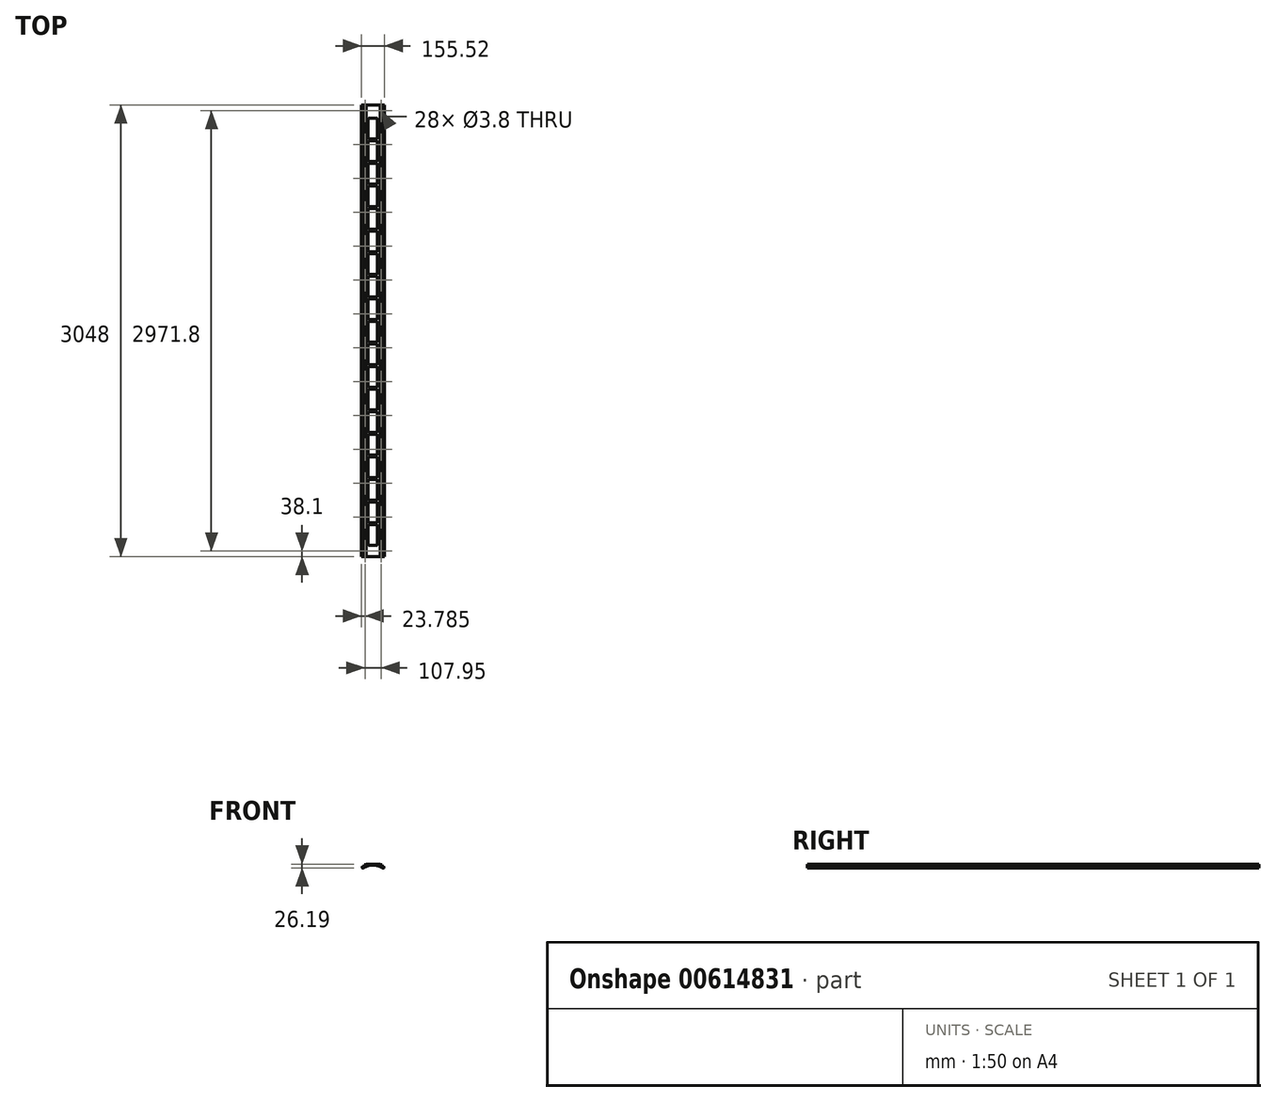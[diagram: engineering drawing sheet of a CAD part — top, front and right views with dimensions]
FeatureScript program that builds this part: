
annotation { "Feature Type Name" : "Feature", "Feature Type Description" : "" }
export const myFeature = defineFeature(function(context is Context, id is Id, definition is map)
    precondition{}
    {
        {
            var Q0;
            Q0=qCreatedBy(makeId("Front.planeOp"),FACE);
            var sketch = newSketch(context, id + "F0", { "sketchPlane" : qUnion([Q0])});
            skLineSegment(sketch, "E0", {"start": v(0, 0) * mm, "end": v(-47.62, 0) * mm});
            skLineSegment(sketch, "E1", {"start": v(-60.33, -4.76) * mm, "end": v(-60.33, -9.52) * mm});
            skArc(sketch, "E2", {"start": v(62.37, -26.2) * mm, "mid": v(0, -6.35) * mm, "end": v(-62.37, -26.2) * mm});
            skLineSegment(sketch, "E3", {"start": v(-60.33, -9.53) * mm, "end": v(-77.76, -22.36) * mm});
            skLineSegment(sketch, "E4", {"start": v(-77.76, -22.36) * mm, "end": v(-73.17, -22.36) * mm});
            skLineSegment(sketch, "E5", {"start": v(-73.17, -22.36) * mm, "end": v(-73.17, -26.2) * mm});
            skLineSegment(sketch, "E6", {"start": v(-73.17, -26.2) * mm, "end": v(-62.37, -26.2) * mm});
            skLineSegment(sketch, "E7.MirrorCS", {"start": v(0, 0) * mm, "end": v(47.62, 0) * mm});
            skLineSegment(sketch, "E8.MirrorCS", {"start": v(60.33, -4.76) * mm, "end": v(60.33, -9.53) * mm});
            skLineSegment(sketch, "E9.MirrorCS", {"start": v(60.33, -9.52) * mm, "end": v(77.76, -22.36) * mm});
            skLineSegment(sketch, "E10.MirrorCS", {"start": v(77.76, -22.36) * mm, "end": v(73.17, -22.36) * mm});
            skLineSegment(sketch, "E11.MirrorCS", {"start": v(73.17, -22.36) * mm, "end": v(73.17, -26.2) * mm});
            skLineSegment(sketch, "E12.MirrorCS", {"start": v(73.17, -26.2) * mm, "end": v(62.37, -26.2) * mm});
            skLineSegment(sketch, "E13", {"start": v(-47.62, 0) * mm, "end": v(-47.62, -4.76) * mm});
            skLineSegment(sketch, "E14", {"start": v(-47.62, -4.76) * mm, "end": v(-60.33, -4.76) * mm});
            skPoint(sketch, "E15.orphan", {"position": v(-60.33, 0) * mm});
            skLineSegment(sketch, "E16.MirrorCS", {"start": v(47.62, 0) * mm, "end": v(47.62, -4.76) * mm});
            skLineSegment(sketch, "E17.MirrorCS", {"start": v(47.62, -4.76) * mm, "end": v(60.33, -4.76) * mm});
            skPoint(sketch, "E18.orphan", {"position": v(60.32, 0) * mm});
            skPoint(sketch, "E19.orphan", {"position": v(60.33, 0) * mm});
            skSolve(sketch);
        }
        {
            var Q0;
            Q0=makeQuery(id+"F0.imprint","IMPRINT",FACE,{"disambiguationData":[TD([[makeQuery(id+"F0.imprint","IMPRINT",EDGE,{"derivedFrom":sQuery(id+"F0.wireOp",EDGE,"E0")}),1.0]])]});
            extrude(context, id + "F1", {"entities" : qUnion([Q0]), "endBound" : BoundingType.SYMMETRIC, "depth" : 3048 * mm, "offsetDistance" : 25.4 * mm});
        }
        {
            var Q0;
            Q0=makeQuery(id+"F1.opExtrude","SWEPT_FACE",FACE,{"disambiguationData":[OSD([sQuery(id+"F0.wireOp",EDGE,"E0"),sQuery(id+"F0.wireOp",EDGE,"E7.MirrorCS")])]});
            var sketch = newSketch(context, id + "F2", { "sketchPlane" : qUnion([Q0])});
            skLineSegment(sketch, "E20.bottom", {"start": v(-32.27, -1447.8) * mm, "end": v(31.23, -1447.8) * mm});
            skLineSegment(sketch, "E20.top", {"start": v(-32.27, -1308.1) * mm, "end": v(31.23, -1308.1) * mm});
            skLineSegment(sketch, "E20.left", {"start": v(-32.27, -1447.8) * mm, "end": v(-32.27, -1308.1) * mm});
            skLineSegment(sketch, "E20.right", {"start": v(31.23, -1447.8) * mm, "end": v(31.23, -1308.1) * mm});
            skLineSegment(sketch, "E21.0.1.0", {"start": v(-32.27, -1295.4) * mm, "end": v(-32.27, -1155.7) * mm});
            skLineSegment(sketch, "E21.0.1.1", {"start": v(-32.27, -1155.7) * mm, "end": v(31.23, -1155.7) * mm});
            skLineSegment(sketch, "E21.0.1.2", {"start": v(31.23, -1295.4) * mm, "end": v(31.23, -1155.7) * mm});
            skLineSegment(sketch, "E21.0.1.3", {"start": v(-32.27, -1295.4) * mm, "end": v(31.23, -1295.4) * mm});
            skLineSegment(sketch, "E21.0.2.0", {"start": v(-32.27, -1143) * mm, "end": v(-32.27, -1003.3) * mm});
            skLineSegment(sketch, "E21.0.2.1", {"start": v(-32.27, -1003.3) * mm, "end": v(31.23, -1003.3) * mm});
            skLineSegment(sketch, "E21.0.2.2", {"start": v(31.23, -1143) * mm, "end": v(31.23, -1003.3) * mm});
            skLineSegment(sketch, "E21.0.2.3", {"start": v(-32.27, -1143) * mm, "end": v(31.23, -1143) * mm});
            skLineSegment(sketch, "E21.0.3.0", {"start": v(-32.27, -990.6) * mm, "end": v(-32.27, -850.9) * mm});
            skLineSegment(sketch, "E21.0.3.1", {"start": v(-32.27, -850.9) * mm, "end": v(31.23, -850.9) * mm});
            skLineSegment(sketch, "E21.0.3.2", {"start": v(31.23, -990.6) * mm, "end": v(31.23, -850.9) * mm});
            skLineSegment(sketch, "E21.0.3.3", {"start": v(-32.27, -990.6) * mm, "end": v(31.23, -990.6) * mm});
            skLineSegment(sketch, "E21.0.4.0", {"start": v(-32.27, -838.2) * mm, "end": v(-32.27, -698.5) * mm});
            skLineSegment(sketch, "E21.0.4.1", {"start": v(-32.27, -698.5) * mm, "end": v(31.23, -698.5) * mm});
            skLineSegment(sketch, "E21.0.4.2", {"start": v(31.23, -838.2) * mm, "end": v(31.23, -698.5) * mm});
            skLineSegment(sketch, "E21.0.4.3", {"start": v(-32.27, -838.2) * mm, "end": v(31.23, -838.2) * mm});
            skLineSegment(sketch, "E21.0.5.0", {"start": v(-32.27, -685.8) * mm, "end": v(-32.27, -546.1) * mm});
            skLineSegment(sketch, "E21.0.5.1", {"start": v(-32.27, -546.1) * mm, "end": v(31.23, -546.1) * mm});
            skLineSegment(sketch, "E21.0.5.2", {"start": v(31.23, -685.8) * mm, "end": v(31.23, -546.1) * mm});
            skLineSegment(sketch, "E21.0.5.3", {"start": v(-32.27, -685.8) * mm, "end": v(31.23, -685.8) * mm});
            skLineSegment(sketch, "E21.0.6.0", {"start": v(-32.27, -533.4) * mm, "end": v(-32.27, -393.7) * mm});
            skLineSegment(sketch, "E21.0.6.1", {"start": v(-32.27, -393.7) * mm, "end": v(31.23, -393.7) * mm});
            skLineSegment(sketch, "E21.0.6.2", {"start": v(31.23, -533.4) * mm, "end": v(31.23, -393.7) * mm});
            skLineSegment(sketch, "E21.0.6.3", {"start": v(-32.27, -533.4) * mm, "end": v(31.23, -533.4) * mm});
            skLineSegment(sketch, "E21.0.7.0", {"start": v(-32.27, -381) * mm, "end": v(-32.27, -241.3) * mm});
            skLineSegment(sketch, "E21.0.7.1", {"start": v(-32.27, -241.3) * mm, "end": v(31.23, -241.3) * mm});
            skLineSegment(sketch, "E21.0.7.2", {"start": v(31.23, -381) * mm, "end": v(31.23, -241.3) * mm});
            skLineSegment(sketch, "E21.0.7.3", {"start": v(-32.27, -381) * mm, "end": v(31.23, -381) * mm});
            skLineSegment(sketch, "E21.0.8.0", {"start": v(-32.27, -228.6) * mm, "end": v(-32.27, -88.9) * mm});
            skLineSegment(sketch, "E21.0.8.1", {"start": v(-32.27, -88.9) * mm, "end": v(31.23, -88.9) * mm});
            skLineSegment(sketch, "E21.0.8.2", {"start": v(31.23, -228.6) * mm, "end": v(31.23, -88.9) * mm});
            skLineSegment(sketch, "E21.0.8.3", {"start": v(-32.27, -228.6) * mm, "end": v(31.23, -228.6) * mm});
            skLineSegment(sketch, "E21.0.9.0", {"start": v(-32.27, -76.2) * mm, "end": v(-32.27, 63.5) * mm});
            skLineSegment(sketch, "E21.0.9.1", {"start": v(-32.27, 63.5) * mm, "end": v(31.23, 63.5) * mm});
            skLineSegment(sketch, "E21.0.9.2", {"start": v(31.23, -76.2) * mm, "end": v(31.23, 63.5) * mm});
            skLineSegment(sketch, "E21.0.9.3", {"start": v(-32.27, -76.2) * mm, "end": v(31.23, -76.2) * mm});
            skLineSegment(sketch, "E21.0.10.0", {"start": v(-32.27, 76.2) * mm, "end": v(-32.27, 215.9) * mm});
            skLineSegment(sketch, "E21.0.10.1", {"start": v(-32.27, 215.9) * mm, "end": v(31.23, 215.9) * mm});
            skLineSegment(sketch, "E21.0.10.2", {"start": v(31.23, 76.2) * mm, "end": v(31.23, 215.9) * mm});
            skLineSegment(sketch, "E21.0.10.3", {"start": v(-32.27, 76.2) * mm, "end": v(31.23, 76.2) * mm});
            skLineSegment(sketch, "E21.0.11.0", {"start": v(-32.27, 228.6) * mm, "end": v(-32.27, 368.3) * mm});
            skLineSegment(sketch, "E21.0.11.1", {"start": v(-32.27, 368.3) * mm, "end": v(31.23, 368.3) * mm});
            skLineSegment(sketch, "E21.0.11.2", {"start": v(31.23, 228.6) * mm, "end": v(31.23, 368.3) * mm});
            skLineSegment(sketch, "E21.0.11.3", {"start": v(-32.27, 228.6) * mm, "end": v(31.23, 228.6) * mm});
            skLineSegment(sketch, "E21.0.12.0", {"start": v(-32.27, 381) * mm, "end": v(-32.27, 520.7) * mm});
            skLineSegment(sketch, "E21.0.12.1", {"start": v(-32.27, 520.7) * mm, "end": v(31.23, 520.7) * mm});
            skLineSegment(sketch, "E21.0.12.2", {"start": v(31.23, 381) * mm, "end": v(31.23, 520.7) * mm});
            skLineSegment(sketch, "E21.0.12.3", {"start": v(-32.27, 381) * mm, "end": v(31.23, 381) * mm});
            skLineSegment(sketch, "E21.0.13.0", {"start": v(-32.27, 533.4) * mm, "end": v(-32.27, 673.1) * mm});
            skLineSegment(sketch, "E21.0.13.1", {"start": v(-32.27, 673.1) * mm, "end": v(31.23, 673.1) * mm});
            skLineSegment(sketch, "E21.0.13.2", {"start": v(31.23, 533.4) * mm, "end": v(31.23, 673.1) * mm});
            skLineSegment(sketch, "E21.0.13.3", {"start": v(-32.27, 533.4) * mm, "end": v(31.23, 533.4) * mm});
            skLineSegment(sketch, "E21.0.14.0", {"start": v(-32.27, 685.8) * mm, "end": v(-32.27, 825.5) * mm});
            skLineSegment(sketch, "E21.0.14.1", {"start": v(-32.27, 825.5) * mm, "end": v(31.23, 825.5) * mm});
            skLineSegment(sketch, "E21.0.14.2", {"start": v(31.23, 685.8) * mm, "end": v(31.23, 825.5) * mm});
            skLineSegment(sketch, "E21.0.14.3", {"start": v(-32.27, 685.8) * mm, "end": v(31.23, 685.8) * mm});
            skLineSegment(sketch, "E21.0.15.0", {"start": v(-32.27, 838.2) * mm, "end": v(-32.27, 977.9) * mm});
            skLineSegment(sketch, "E21.0.15.1", {"start": v(-32.27, 977.9) * mm, "end": v(31.23, 977.9) * mm});
            skLineSegment(sketch, "E21.0.15.2", {"start": v(31.23, 838.2) * mm, "end": v(31.23, 977.9) * mm});
            skLineSegment(sketch, "E21.0.15.3", {"start": v(-32.27, 838.2) * mm, "end": v(31.23, 838.2) * mm});
            skLineSegment(sketch, "E21.0.16.0", {"start": v(-32.27, 990.6) * mm, "end": v(-32.27, 1130.3) * mm});
            skLineSegment(sketch, "E21.0.16.1", {"start": v(-32.27, 1130.3) * mm, "end": v(31.23, 1130.3) * mm});
            skLineSegment(sketch, "E21.0.16.2", {"start": v(31.23, 990.6) * mm, "end": v(31.23, 1130.3) * mm});
            skLineSegment(sketch, "E21.0.16.3", {"start": v(-32.27, 990.6) * mm, "end": v(31.23, 990.6) * mm});
            skLineSegment(sketch, "E21.0.17.0", {"start": v(-32.27, 1143) * mm, "end": v(-32.27, 1282.7) * mm});
            skLineSegment(sketch, "E21.0.17.1", {"start": v(-32.27, 1282.7) * mm, "end": v(31.23, 1282.7) * mm});
            skLineSegment(sketch, "E21.0.17.2", {"start": v(31.23, 1143) * mm, "end": v(31.23, 1282.7) * mm});
            skLineSegment(sketch, "E21.0.17.3", {"start": v(-32.27, 1143) * mm, "end": v(31.23, 1143) * mm});
            skLineSegment(sketch, "E21.0.18.0", {"start": v(-32.27, 1295.4) * mm, "end": v(-32.27, 1435.1) * mm});
            skLineSegment(sketch, "E21.0.18.1", {"start": v(-32.27, 1435.1) * mm, "end": v(31.23, 1435.1) * mm});
            skLineSegment(sketch, "E21.0.18.2", {"start": v(31.23, 1295.4) * mm, "end": v(31.23, 1435.1) * mm});
            skLineSegment(sketch, "E21.0.18.3", {"start": v(-32.27, 1295.4) * mm, "end": v(31.23, 1295.4) * mm});
            skLineSegment(sketch, "E21.0.19.0", {"start": v(-32.27, 1447.8) * mm, "end": v(-32.27, 1587.5) * mm});
            skLineSegment(sketch, "E21.0.19.1", {"start": v(-32.27, 1587.5) * mm, "end": v(31.23, 1587.5) * mm});
            skLineSegment(sketch, "E21.0.19.2", {"start": v(31.23, 1447.8) * mm, "end": v(31.23, 1587.5) * mm});
            skLineSegment(sketch, "E21.0.19.3", {"start": v(-32.27, 1447.8) * mm, "end": v(31.23, 1447.8) * mm});
            skLineSegment(sketch, "E21.direction1", {"start": v(-32.27, -1447.8) * mm, "end": v(-6.87, -1447.8) * mm, "construction": true});
            skLineSegment(sketch, "E21.direction2", {"start": v(-32.27, -1447.8) * mm, "end": v(-32.27, -1295.4) * mm, "construction": true});
            skSolve(sketch);
        }
        {
            var Q0;
            Q0=makeQuery(id+"F2.imprint","IMPRINT",FACE,{"disambiguationData":[TD([[makeQuery(id+"F2.imprint","IMPRINT",EDGE,{"derivedFrom":sQuery(id+"F2.wireOp",EDGE,"E20.bottom")}),1.0]])]});
            var Q1;
            Q1=makeQuery(id+"F2.imprint","IMPRINT",FACE,{"disambiguationData":[TD([[makeQuery(id+"F2.imprint","IMPRINT",EDGE,{"derivedFrom":sQuery(id+"F2.wireOp",EDGE,"E21.0.1.0")}),-1.0]])]});
            var Q2;
            Q2=makeQuery(id+"F2.imprint","IMPRINT",FACE,{"disambiguationData":[TD([[makeQuery(id+"F2.imprint","IMPRINT",EDGE,{"derivedFrom":sQuery(id+"F2.wireOp",EDGE,"E21.0.2.0")}),-1.0]])]});
            var Q3;
            Q3=makeQuery(id+"F2.imprint","IMPRINT",FACE,{"disambiguationData":[TD([[makeQuery(id+"F2.imprint","IMPRINT",EDGE,{"derivedFrom":sQuery(id+"F2.wireOp",EDGE,"E21.0.3.0")}),-1.0]])]});
            var Q4;
            Q4=makeQuery(id+"F2.imprint","IMPRINT",FACE,{"disambiguationData":[TD([[makeQuery(id+"F2.imprint","IMPRINT",EDGE,{"derivedFrom":sQuery(id+"F2.wireOp",EDGE,"E21.0.4.0")}),-1.0]])]});
            var Q5;
            Q5=makeQuery(id+"F2.imprint","IMPRINT",FACE,{"disambiguationData":[TD([[makeQuery(id+"F2.imprint","IMPRINT",EDGE,{"derivedFrom":sQuery(id+"F2.wireOp",EDGE,"E21.0.5.0")}),-1.0]])]});
            var Q6;
            Q6=makeQuery(id+"F2.imprint","IMPRINT",FACE,{"disambiguationData":[TD([[makeQuery(id+"F2.imprint","IMPRINT",EDGE,{"derivedFrom":sQuery(id+"F2.wireOp",EDGE,"E21.0.6.0")}),-1.0]])]});
            var Q7;
            Q7=makeQuery(id+"F2.imprint","IMPRINT",FACE,{"disambiguationData":[TD([[makeQuery(id+"F2.imprint","IMPRINT",EDGE,{"derivedFrom":sQuery(id+"F2.wireOp",EDGE,"E21.0.7.0")}),-1.0]])]});
            var Q8;
            Q8=makeQuery(id+"F2.imprint","IMPRINT",FACE,{"disambiguationData":[TD([[makeQuery(id+"F2.imprint","IMPRINT",EDGE,{"derivedFrom":sQuery(id+"F2.wireOp",EDGE,"E21.0.8.0")}),-1.0]])]});
            var Q9;
            Q9=makeQuery(id+"F2.imprint","IMPRINT",FACE,{"disambiguationData":[TD([[makeQuery(id+"F2.imprint","IMPRINT",EDGE,{"derivedFrom":sQuery(id+"F2.wireOp",EDGE,"E21.0.9.0")}),-1.0]])]});
            var Q10;
            Q10=makeQuery(id+"F2.imprint","IMPRINT",FACE,{"disambiguationData":[TD([[makeQuery(id+"F2.imprint","IMPRINT",EDGE,{"derivedFrom":sQuery(id+"F2.wireOp",EDGE,"E21.0.10.0")}),-1.0]])]});
            var Q11;
            Q11=makeQuery(id+"F2.imprint","IMPRINT",FACE,{"disambiguationData":[TD([[makeQuery(id+"F2.imprint","IMPRINT",EDGE,{"derivedFrom":sQuery(id+"F2.wireOp",EDGE,"E21.0.11.0")}),-1.0]])]});
            var Q12;
            Q12=makeQuery(id+"F2.imprint","IMPRINT",FACE,{"disambiguationData":[TD([[makeQuery(id+"F2.imprint","IMPRINT",EDGE,{"derivedFrom":sQuery(id+"F2.wireOp",EDGE,"E21.0.12.0")}),-1.0]])]});
            var Q13;
            Q13=makeQuery(id+"F2.imprint","IMPRINT",FACE,{"disambiguationData":[TD([[makeQuery(id+"F2.imprint","IMPRINT",EDGE,{"derivedFrom":sQuery(id+"F2.wireOp",EDGE,"E21.0.13.0")}),-1.0]])]});
            var Q14;
            Q14=makeQuery(id+"F2.imprint","IMPRINT",FACE,{"disambiguationData":[TD([[makeQuery(id+"F2.imprint","IMPRINT",EDGE,{"derivedFrom":sQuery(id+"F2.wireOp",EDGE,"E21.0.14.0")}),-1.0]])]});
            var Q15;
            Q15=makeQuery(id+"F2.imprint","IMPRINT",FACE,{"disambiguationData":[TD([[makeQuery(id+"F2.imprint","IMPRINT",EDGE,{"derivedFrom":sQuery(id+"F2.wireOp",EDGE,"E21.0.15.0")}),-1.0]])]});
            var Q16;
            Q16=makeQuery(id+"F2.imprint","IMPRINT",FACE,{"disambiguationData":[TD([[makeQuery(id+"F2.imprint","IMPRINT",EDGE,{"derivedFrom":sQuery(id+"F2.wireOp",EDGE,"E21.0.16.0")}),-1.0]])]});
            var Q17;
            Q17=makeQuery(id+"F2.imprint","IMPRINT",FACE,{"disambiguationData":[TD([[makeQuery(id+"F2.imprint","IMPRINT",EDGE,{"derivedFrom":sQuery(id+"F2.wireOp",EDGE,"E21.0.17.0")}),-1.0]])]});
            var Q18;
            Q18=makeQuery(id+"F2.imprint","IMPRINT",FACE,{"disambiguationData":[TD([[makeQuery(id+"F2.imprint","IMPRINT",EDGE,{"derivedFrom":sQuery(id+"F2.wireOp",EDGE,"E21.0.18.0")}),-1.0]])]});
            extrude(context, id + "F3", {"entities" : qUnion([Q0, Q1, Q2, Q3, Q4, Q5, Q6, Q7, Q8, Q9, Q10, Q11, Q12, Q13, Q14, Q15, Q16, Q17, Q18]), "operationType" : NewBodyOperationType.REMOVE, "oppositeDirection" : true, "depth" : 25.4 * mm, "offsetDistance" : 25.4 * mm});
        }
        {
            var Q0;
            Q0=makeQuery(id+"F3.boolean.opBoolean","COPY",EDGE,{"derivedFrom":makeQuery(id+"F3.opExtrude","SWEPT_EDGE",EDGE,{"disambiguationData":[OSD([sQuery(id+"F2.wireOp",EDGE,"E20.top"),sQuery(id+"F2.wireOp",EDGE,"E20.right")])]})});
            var Q1;
            Q1=makeQuery(id+"F3.boolean.opBoolean","COPY",EDGE,{"derivedFrom":makeQuery(id+"F3.opExtrude","SWEPT_EDGE",EDGE,{"disambiguationData":[OSD([sQuery(id+"F2.wireOp",EDGE,"E20.top"),sQuery(id+"F2.wireOp",EDGE,"E20.left")])]})});
            var Q2;
            Q2=makeQuery(id+"F3.boolean.opBoolean","COPY",EDGE,{"derivedFrom":makeQuery(id+"F3.opExtrude","SWEPT_EDGE",EDGE,{"disambiguationData":[OSD([sQuery(id+"F2.wireOp",EDGE,"E20.bottom"),sQuery(id+"F2.wireOp",EDGE,"E20.left")])]})});
            var Q3;
            Q3=makeQuery(id+"F3.boolean.opBoolean","COPY",EDGE,{"derivedFrom":makeQuery(id+"F3.opExtrude","SWEPT_EDGE",EDGE,{"disambiguationData":[OSD([sQuery(id+"F2.wireOp",EDGE,"E20.bottom"),sQuery(id+"F2.wireOp",EDGE,"E20.right")])]})});
            var Q4;
            Q4=makeQuery(id+"F3.boolean.opBoolean","COPY",EDGE,{"derivedFrom":makeQuery(id+"F3.opExtrude","SWEPT_EDGE",EDGE,{"disambiguationData":[OSD([sQuery(id+"F2.wireOp",EDGE,"E21.0.1.2"),sQuery(id+"F2.wireOp",EDGE,"E21.0.1.3")])]})});
            var Q5;
            Q5=makeQuery(id+"F3.boolean.opBoolean","COPY",EDGE,{"derivedFrom":makeQuery(id+"F3.opExtrude","SWEPT_EDGE",EDGE,{"disambiguationData":[OSD([sQuery(id+"F2.wireOp",EDGE,"E21.0.2.2"),sQuery(id+"F2.wireOp",EDGE,"E21.0.2.3")])]})});
            var Q6;
            Q6=makeQuery(id+"F3.boolean.opBoolean","COPY",EDGE,{"derivedFrom":makeQuery(id+"F3.opExtrude","SWEPT_EDGE",EDGE,{"disambiguationData":[OSD([sQuery(id+"F2.wireOp",EDGE,"E21.0.3.2"),sQuery(id+"F2.wireOp",EDGE,"E21.0.3.3")])]})});
            var Q7;
            Q7=makeQuery(id+"F3.boolean.opBoolean","COPY",EDGE,{"derivedFrom":makeQuery(id+"F3.opExtrude","SWEPT_EDGE",EDGE,{"disambiguationData":[OSD([sQuery(id+"F2.wireOp",EDGE,"E21.0.4.2"),sQuery(id+"F2.wireOp",EDGE,"E21.0.4.3")])]})});
            var Q8;
            Q8=makeQuery(id+"F3.boolean.opBoolean","COPY",EDGE,{"derivedFrom":makeQuery(id+"F3.opExtrude","SWEPT_EDGE",EDGE,{"disambiguationData":[OSD([sQuery(id+"F2.wireOp",EDGE,"E21.0.5.2"),sQuery(id+"F2.wireOp",EDGE,"E21.0.5.3")])]})});
            var Q9;
            Q9=makeQuery(id+"F3.boolean.opBoolean","COPY",EDGE,{"derivedFrom":makeQuery(id+"F3.opExtrude","SWEPT_EDGE",EDGE,{"disambiguationData":[OSD([sQuery(id+"F2.wireOp",EDGE,"E21.0.6.2"),sQuery(id+"F2.wireOp",EDGE,"E21.0.6.3")])]})});
            var Q10;
            Q10=makeQuery(id+"F3.boolean.opBoolean","COPY",EDGE,{"derivedFrom":makeQuery(id+"F3.opExtrude","SWEPT_EDGE",EDGE,{"disambiguationData":[OSD([sQuery(id+"F2.wireOp",EDGE,"E21.0.7.2"),sQuery(id+"F2.wireOp",EDGE,"E21.0.7.3")])]})});
            var Q11;
            Q11=makeQuery(id+"F3.boolean.opBoolean","COPY",EDGE,{"derivedFrom":makeQuery(id+"F3.opExtrude","SWEPT_EDGE",EDGE,{"disambiguationData":[OSD([sQuery(id+"F2.wireOp",EDGE,"E21.0.8.2"),sQuery(id+"F2.wireOp",EDGE,"E21.0.8.3")])]})});
            var Q12;
            Q12=makeQuery(id+"F3.boolean.opBoolean","COPY",EDGE,{"derivedFrom":makeQuery(id+"F3.opExtrude","SWEPT_EDGE",EDGE,{"disambiguationData":[OSD([sQuery(id+"F2.wireOp",EDGE,"E21.0.9.2"),sQuery(id+"F2.wireOp",EDGE,"E21.0.9.3")])]})});
            var Q13;
            Q13=makeQuery(id+"F3.boolean.opBoolean","COPY",EDGE,{"derivedFrom":makeQuery(id+"F3.opExtrude","SWEPT_EDGE",EDGE,{"disambiguationData":[OSD([sQuery(id+"F2.wireOp",EDGE,"E21.0.10.2"),sQuery(id+"F2.wireOp",EDGE,"E21.0.10.3")])]})});
            var Q14;
            Q14=makeQuery(id+"F3.boolean.opBoolean","COPY",EDGE,{"derivedFrom":makeQuery(id+"F3.opExtrude","SWEPT_EDGE",EDGE,{"disambiguationData":[OSD([sQuery(id+"F2.wireOp",EDGE,"E21.0.11.2"),sQuery(id+"F2.wireOp",EDGE,"E21.0.11.3")])]})});
            var Q15;
            Q15=makeQuery(id+"F3.boolean.opBoolean","COPY",EDGE,{"derivedFrom":makeQuery(id+"F3.opExtrude","SWEPT_EDGE",EDGE,{"disambiguationData":[OSD([sQuery(id+"F2.wireOp",EDGE,"E21.0.12.2"),sQuery(id+"F2.wireOp",EDGE,"E21.0.12.3")])]})});
            var Q16;
            Q16=makeQuery(id+"F3.boolean.opBoolean","COPY",EDGE,{"derivedFrom":makeQuery(id+"F3.opExtrude","SWEPT_EDGE",EDGE,{"disambiguationData":[OSD([sQuery(id+"F2.wireOp",EDGE,"E21.0.13.2"),sQuery(id+"F2.wireOp",EDGE,"E21.0.13.3")])]})});
            var Q17;
            Q17=makeQuery(id+"F3.boolean.opBoolean","COPY",EDGE,{"derivedFrom":makeQuery(id+"F3.opExtrude","SWEPT_EDGE",EDGE,{"disambiguationData":[OSD([sQuery(id+"F2.wireOp",EDGE,"E21.0.14.2"),sQuery(id+"F2.wireOp",EDGE,"E21.0.14.3")])]})});
            var Q18;
            Q18=makeQuery(id+"F3.boolean.opBoolean","COPY",EDGE,{"derivedFrom":makeQuery(id+"F3.opExtrude","SWEPT_EDGE",EDGE,{"disambiguationData":[OSD([sQuery(id+"F2.wireOp",EDGE,"E21.0.15.2"),sQuery(id+"F2.wireOp",EDGE,"E21.0.15.3")])]})});
            var Q19;
            Q19=makeQuery(id+"F3.boolean.opBoolean","COPY",EDGE,{"derivedFrom":makeQuery(id+"F3.opExtrude","SWEPT_EDGE",EDGE,{"disambiguationData":[OSD([sQuery(id+"F2.wireOp",EDGE,"E21.0.16.2"),sQuery(id+"F2.wireOp",EDGE,"E21.0.16.3")])]})});
            var Q20;
            Q20=makeQuery(id+"F3.boolean.opBoolean","COPY",EDGE,{"derivedFrom":makeQuery(id+"F3.opExtrude","SWEPT_EDGE",EDGE,{"disambiguationData":[OSD([sQuery(id+"F2.wireOp",EDGE,"E21.0.17.2"),sQuery(id+"F2.wireOp",EDGE,"E21.0.17.3")])]})});
            var Q21;
            Q21=makeQuery(id+"F3.boolean.opBoolean","COPY",EDGE,{"derivedFrom":makeQuery(id+"F3.opExtrude","SWEPT_EDGE",EDGE,{"disambiguationData":[OSD([sQuery(id+"F2.wireOp",EDGE,"E21.0.18.2"),sQuery(id+"F2.wireOp",EDGE,"E21.0.18.3")])]})});
            var Q22;
            Q22=makeQuery(id+"F3.boolean.opBoolean","COPY",EDGE,{"derivedFrom":makeQuery(id+"F3.opExtrude","SWEPT_EDGE",EDGE,{"disambiguationData":[OSD([sQuery(id+"F2.wireOp",EDGE,"E21.0.18.1"),sQuery(id+"F2.wireOp",EDGE,"E21.0.18.2")])]})});
            var Q23;
            Q23=makeQuery(id+"F3.boolean.opBoolean","COPY",EDGE,{"derivedFrom":makeQuery(id+"F3.opExtrude","SWEPT_EDGE",EDGE,{"disambiguationData":[OSD([sQuery(id+"F2.wireOp",EDGE,"E21.0.17.1"),sQuery(id+"F2.wireOp",EDGE,"E21.0.17.2")])]})});
            var Q24;
            Q24=makeQuery(id+"F3.boolean.opBoolean","COPY",EDGE,{"derivedFrom":makeQuery(id+"F3.opExtrude","SWEPT_EDGE",EDGE,{"disambiguationData":[OSD([sQuery(id+"F2.wireOp",EDGE,"E21.0.16.1"),sQuery(id+"F2.wireOp",EDGE,"E21.0.16.2")])]})});
            var Q25;
            Q25=makeQuery(id+"F3.boolean.opBoolean","COPY",EDGE,{"derivedFrom":makeQuery(id+"F3.opExtrude","SWEPT_EDGE",EDGE,{"disambiguationData":[OSD([sQuery(id+"F2.wireOp",EDGE,"E21.0.15.1"),sQuery(id+"F2.wireOp",EDGE,"E21.0.15.2")])]})});
            var Q26;
            Q26=makeQuery(id+"F3.boolean.opBoolean","COPY",EDGE,{"derivedFrom":makeQuery(id+"F3.opExtrude","SWEPT_EDGE",EDGE,{"disambiguationData":[OSD([sQuery(id+"F2.wireOp",EDGE,"E21.0.14.1"),sQuery(id+"F2.wireOp",EDGE,"E21.0.14.2")])]})});
            var Q27;
            Q27=makeQuery(id+"F3.boolean.opBoolean","COPY",EDGE,{"derivedFrom":makeQuery(id+"F3.opExtrude","SWEPT_EDGE",EDGE,{"disambiguationData":[OSD([sQuery(id+"F2.wireOp",EDGE,"E21.0.13.1"),sQuery(id+"F2.wireOp",EDGE,"E21.0.13.2")])]})});
            var Q28;
            Q28=makeQuery(id+"F3.boolean.opBoolean","COPY",EDGE,{"derivedFrom":makeQuery(id+"F3.opExtrude","SWEPT_EDGE",EDGE,{"disambiguationData":[OSD([sQuery(id+"F2.wireOp",EDGE,"E21.0.12.1"),sQuery(id+"F2.wireOp",EDGE,"E21.0.12.2")])]})});
            var Q29;
            Q29=makeQuery(id+"F3.boolean.opBoolean","COPY",EDGE,{"derivedFrom":makeQuery(id+"F3.opExtrude","SWEPT_EDGE",EDGE,{"disambiguationData":[OSD([sQuery(id+"F2.wireOp",EDGE,"E21.0.11.1"),sQuery(id+"F2.wireOp",EDGE,"E21.0.11.2")])]})});
            var Q30;
            Q30=makeQuery(id+"F3.boolean.opBoolean","COPY",EDGE,{"derivedFrom":makeQuery(id+"F3.opExtrude","SWEPT_EDGE",EDGE,{"disambiguationData":[OSD([sQuery(id+"F2.wireOp",EDGE,"E21.0.10.1"),sQuery(id+"F2.wireOp",EDGE,"E21.0.10.2")])]})});
            var Q31;
            Q31=makeQuery(id+"F3.boolean.opBoolean","COPY",EDGE,{"derivedFrom":makeQuery(id+"F3.opExtrude","SWEPT_EDGE",EDGE,{"disambiguationData":[OSD([sQuery(id+"F2.wireOp",EDGE,"E21.0.9.1"),sQuery(id+"F2.wireOp",EDGE,"E21.0.9.2")])]})});
            var Q32;
            Q32=makeQuery(id+"F3.boolean.opBoolean","COPY",EDGE,{"derivedFrom":makeQuery(id+"F3.opExtrude","SWEPT_EDGE",EDGE,{"disambiguationData":[OSD([sQuery(id+"F2.wireOp",EDGE,"E21.0.8.1"),sQuery(id+"F2.wireOp",EDGE,"E21.0.8.2")])]})});
            var Q33;
            Q33=makeQuery(id+"F3.boolean.opBoolean","COPY",EDGE,{"derivedFrom":makeQuery(id+"F3.opExtrude","SWEPT_EDGE",EDGE,{"disambiguationData":[OSD([sQuery(id+"F2.wireOp",EDGE,"E21.0.7.1"),sQuery(id+"F2.wireOp",EDGE,"E21.0.7.2")])]})});
            var Q34;
            Q34=makeQuery(id+"F3.boolean.opBoolean","COPY",EDGE,{"derivedFrom":makeQuery(id+"F3.opExtrude","SWEPT_EDGE",EDGE,{"disambiguationData":[OSD([sQuery(id+"F2.wireOp",EDGE,"E21.0.6.1"),sQuery(id+"F2.wireOp",EDGE,"E21.0.6.2")])]})});
            var Q35;
            Q35=makeQuery(id+"F3.boolean.opBoolean","COPY",EDGE,{"derivedFrom":makeQuery(id+"F3.opExtrude","SWEPT_EDGE",EDGE,{"disambiguationData":[OSD([sQuery(id+"F2.wireOp",EDGE,"E21.0.5.1"),sQuery(id+"F2.wireOp",EDGE,"E21.0.5.2")])]})});
            var Q36;
            Q36=makeQuery(id+"F3.boolean.opBoolean","COPY",EDGE,{"derivedFrom":makeQuery(id+"F3.opExtrude","SWEPT_EDGE",EDGE,{"disambiguationData":[OSD([sQuery(id+"F2.wireOp",EDGE,"E21.0.4.1"),sQuery(id+"F2.wireOp",EDGE,"E21.0.4.2")])]})});
            var Q37;
            Q37=makeQuery(id+"F3.boolean.opBoolean","COPY",EDGE,{"derivedFrom":makeQuery(id+"F3.opExtrude","SWEPT_EDGE",EDGE,{"disambiguationData":[OSD([sQuery(id+"F2.wireOp",EDGE,"E21.0.3.1"),sQuery(id+"F2.wireOp",EDGE,"E21.0.3.2")])]})});
            var Q38;
            Q38=makeQuery(id+"F3.boolean.opBoolean","COPY",EDGE,{"derivedFrom":makeQuery(id+"F3.opExtrude","SWEPT_EDGE",EDGE,{"disambiguationData":[OSD([sQuery(id+"F2.wireOp",EDGE,"E21.0.2.1"),sQuery(id+"F2.wireOp",EDGE,"E21.0.2.2")])]})});
            var Q39;
            Q39=makeQuery(id+"F3.boolean.opBoolean","COPY",EDGE,{"derivedFrom":makeQuery(id+"F3.opExtrude","SWEPT_EDGE",EDGE,{"disambiguationData":[OSD([sQuery(id+"F2.wireOp",EDGE,"E21.0.1.1"),sQuery(id+"F2.wireOp",EDGE,"E21.0.1.2")])]})});
            var Q40;
            Q40=makeQuery(id+"F3.boolean.opBoolean","COPY",EDGE,{"derivedFrom":makeQuery(id+"F3.opExtrude","SWEPT_EDGE",EDGE,{"disambiguationData":[OSD([sQuery(id+"F2.wireOp",EDGE,"E21.0.1.0"),sQuery(id+"F2.wireOp",EDGE,"E21.0.1.1")])]})});
            var Q41;
            Q41=makeQuery(id+"F3.boolean.opBoolean","COPY",EDGE,{"derivedFrom":makeQuery(id+"F3.opExtrude","SWEPT_EDGE",EDGE,{"disambiguationData":[OSD([sQuery(id+"F2.wireOp",EDGE,"E21.0.2.0"),sQuery(id+"F2.wireOp",EDGE,"E21.0.2.1")])]})});
            var Q42;
            Q42=makeQuery(id+"F3.boolean.opBoolean","COPY",EDGE,{"derivedFrom":makeQuery(id+"F3.opExtrude","SWEPT_EDGE",EDGE,{"disambiguationData":[OSD([sQuery(id+"F2.wireOp",EDGE,"E21.0.3.0"),sQuery(id+"F2.wireOp",EDGE,"E21.0.3.1")])]})});
            var Q43;
            Q43=makeQuery(id+"F3.boolean.opBoolean","COPY",EDGE,{"derivedFrom":makeQuery(id+"F3.opExtrude","SWEPT_EDGE",EDGE,{"disambiguationData":[OSD([sQuery(id+"F2.wireOp",EDGE,"E21.0.4.0"),sQuery(id+"F2.wireOp",EDGE,"E21.0.4.1")])]})});
            var Q44;
            Q44=makeQuery(id+"F3.boolean.opBoolean","COPY",EDGE,{"derivedFrom":makeQuery(id+"F3.opExtrude","SWEPT_EDGE",EDGE,{"disambiguationData":[OSD([sQuery(id+"F2.wireOp",EDGE,"E21.0.5.0"),sQuery(id+"F2.wireOp",EDGE,"E21.0.5.1")])]})});
            var Q45;
            Q45=makeQuery(id+"F3.boolean.opBoolean","COPY",EDGE,{"derivedFrom":makeQuery(id+"F3.opExtrude","SWEPT_EDGE",EDGE,{"disambiguationData":[OSD([sQuery(id+"F2.wireOp",EDGE,"E21.0.6.0"),sQuery(id+"F2.wireOp",EDGE,"E21.0.6.1")])]})});
            var Q46;
            Q46=makeQuery(id+"F3.boolean.opBoolean","COPY",EDGE,{"derivedFrom":makeQuery(id+"F3.opExtrude","SWEPT_EDGE",EDGE,{"disambiguationData":[OSD([sQuery(id+"F2.wireOp",EDGE,"E21.0.7.0"),sQuery(id+"F2.wireOp",EDGE,"E21.0.7.1")])]})});
            var Q47;
            Q47=makeQuery(id+"F3.boolean.opBoolean","COPY",EDGE,{"derivedFrom":makeQuery(id+"F3.opExtrude","SWEPT_EDGE",EDGE,{"disambiguationData":[OSD([sQuery(id+"F2.wireOp",EDGE,"E21.0.8.0"),sQuery(id+"F2.wireOp",EDGE,"E21.0.8.1")])]})});
            var Q48;
            Q48=makeQuery(id+"F3.boolean.opBoolean","COPY",EDGE,{"derivedFrom":makeQuery(id+"F3.opExtrude","SWEPT_EDGE",EDGE,{"disambiguationData":[OSD([sQuery(id+"F2.wireOp",EDGE,"E21.0.9.0"),sQuery(id+"F2.wireOp",EDGE,"E21.0.9.1")])]})});
            var Q49;
            Q49=makeQuery(id+"F3.boolean.opBoolean","COPY",EDGE,{"derivedFrom":makeQuery(id+"F3.opExtrude","SWEPT_EDGE",EDGE,{"disambiguationData":[OSD([sQuery(id+"F2.wireOp",EDGE,"E21.0.10.0"),sQuery(id+"F2.wireOp",EDGE,"E21.0.10.1")])]})});
            var Q50;
            Q50=makeQuery(id+"F3.boolean.opBoolean","COPY",EDGE,{"derivedFrom":makeQuery(id+"F3.opExtrude","SWEPT_EDGE",EDGE,{"disambiguationData":[OSD([sQuery(id+"F2.wireOp",EDGE,"E21.0.11.0"),sQuery(id+"F2.wireOp",EDGE,"E21.0.11.1")])]})});
            var Q51;
            Q51=makeQuery(id+"F3.boolean.opBoolean","COPY",EDGE,{"derivedFrom":makeQuery(id+"F3.opExtrude","SWEPT_EDGE",EDGE,{"disambiguationData":[OSD([sQuery(id+"F2.wireOp",EDGE,"E21.0.12.0"),sQuery(id+"F2.wireOp",EDGE,"E21.0.12.1")])]})});
            var Q52;
            Q52=makeQuery(id+"F3.boolean.opBoolean","COPY",EDGE,{"derivedFrom":makeQuery(id+"F3.opExtrude","SWEPT_EDGE",EDGE,{"disambiguationData":[OSD([sQuery(id+"F2.wireOp",EDGE,"E21.0.13.0"),sQuery(id+"F2.wireOp",EDGE,"E21.0.13.1")])]})});
            var Q53;
            Q53=makeQuery(id+"F3.boolean.opBoolean","COPY",EDGE,{"derivedFrom":makeQuery(id+"F3.opExtrude","SWEPT_EDGE",EDGE,{"disambiguationData":[OSD([sQuery(id+"F2.wireOp",EDGE,"E21.0.14.0"),sQuery(id+"F2.wireOp",EDGE,"E21.0.14.1")])]})});
            var Q54;
            Q54=makeQuery(id+"F3.boolean.opBoolean","COPY",EDGE,{"derivedFrom":makeQuery(id+"F3.opExtrude","SWEPT_EDGE",EDGE,{"disambiguationData":[OSD([sQuery(id+"F2.wireOp",EDGE,"E21.0.15.0"),sQuery(id+"F2.wireOp",EDGE,"E21.0.15.1")])]})});
            var Q55;
            Q55=makeQuery(id+"F3.boolean.opBoolean","COPY",EDGE,{"derivedFrom":makeQuery(id+"F3.opExtrude","SWEPT_EDGE",EDGE,{"disambiguationData":[OSD([sQuery(id+"F2.wireOp",EDGE,"E21.0.18.0"),sQuery(id+"F2.wireOp",EDGE,"E21.0.18.1")])]})});
            var Q56;
            Q56=makeQuery(id+"F3.boolean.opBoolean","COPY",EDGE,{"derivedFrom":makeQuery(id+"F3.opExtrude","SWEPT_EDGE",EDGE,{"disambiguationData":[OSD([sQuery(id+"F2.wireOp",EDGE,"E21.0.17.0"),sQuery(id+"F2.wireOp",EDGE,"E21.0.17.1")])]})});
            var Q57;
            Q57=makeQuery(id+"F3.boolean.opBoolean","COPY",EDGE,{"derivedFrom":makeQuery(id+"F3.opExtrude","SWEPT_EDGE",EDGE,{"disambiguationData":[OSD([sQuery(id+"F2.wireOp",EDGE,"E21.0.16.0"),sQuery(id+"F2.wireOp",EDGE,"E21.0.16.1")])]})});
            var Q58;
            Q58=makeQuery(id+"F3.boolean.opBoolean","COPY",EDGE,{"derivedFrom":makeQuery(id+"F3.opExtrude","SWEPT_EDGE",EDGE,{"disambiguationData":[OSD([sQuery(id+"F2.wireOp",EDGE,"E21.0.18.0"),sQuery(id+"F2.wireOp",EDGE,"E21.0.18.3")])]})});
            var Q59;
            Q59=makeQuery(id+"F3.boolean.opBoolean","COPY",EDGE,{"derivedFrom":makeQuery(id+"F3.opExtrude","SWEPT_EDGE",EDGE,{"disambiguationData":[OSD([sQuery(id+"F2.wireOp",EDGE,"E21.0.17.0"),sQuery(id+"F2.wireOp",EDGE,"E21.0.17.3")])]})});
            var Q60;
            Q60=makeQuery(id+"F3.boolean.opBoolean","COPY",EDGE,{"derivedFrom":makeQuery(id+"F3.opExtrude","SWEPT_EDGE",EDGE,{"disambiguationData":[OSD([sQuery(id+"F2.wireOp",EDGE,"E21.0.16.0"),sQuery(id+"F2.wireOp",EDGE,"E21.0.16.3")])]})});
            var Q61;
            Q61=makeQuery(id+"F3.boolean.opBoolean","COPY",EDGE,{"derivedFrom":makeQuery(id+"F3.opExtrude","SWEPT_EDGE",EDGE,{"disambiguationData":[OSD([sQuery(id+"F2.wireOp",EDGE,"E21.0.15.0"),sQuery(id+"F2.wireOp",EDGE,"E21.0.15.3")])]})});
            var Q62;
            Q62=makeQuery(id+"F3.boolean.opBoolean","COPY",EDGE,{"derivedFrom":makeQuery(id+"F3.opExtrude","SWEPT_EDGE",EDGE,{"disambiguationData":[OSD([sQuery(id+"F2.wireOp",EDGE,"E21.0.14.0"),sQuery(id+"F2.wireOp",EDGE,"E21.0.14.3")])]})});
            var Q63;
            Q63=makeQuery(id+"F3.boolean.opBoolean","COPY",EDGE,{"derivedFrom":makeQuery(id+"F3.opExtrude","SWEPT_EDGE",EDGE,{"disambiguationData":[OSD([sQuery(id+"F2.wireOp",EDGE,"E21.0.13.0"),sQuery(id+"F2.wireOp",EDGE,"E21.0.13.3")])]})});
            var Q64;
            Q64=makeQuery(id+"F3.boolean.opBoolean","COPY",EDGE,{"derivedFrom":makeQuery(id+"F3.opExtrude","SWEPT_EDGE",EDGE,{"disambiguationData":[OSD([sQuery(id+"F2.wireOp",EDGE,"E21.0.12.0"),sQuery(id+"F2.wireOp",EDGE,"E21.0.12.3")])]})});
            var Q65;
            Q65=makeQuery(id+"F3.boolean.opBoolean","COPY",EDGE,{"derivedFrom":makeQuery(id+"F3.opExtrude","SWEPT_EDGE",EDGE,{"disambiguationData":[OSD([sQuery(id+"F2.wireOp",EDGE,"E21.0.11.0"),sQuery(id+"F2.wireOp",EDGE,"E21.0.11.3")])]})});
            var Q66;
            Q66=makeQuery(id+"F3.boolean.opBoolean","COPY",EDGE,{"derivedFrom":makeQuery(id+"F3.opExtrude","SWEPT_EDGE",EDGE,{"disambiguationData":[OSD([sQuery(id+"F2.wireOp",EDGE,"E21.0.10.0"),sQuery(id+"F2.wireOp",EDGE,"E21.0.10.3")])]})});
            var Q67;
            Q67=makeQuery(id+"F3.boolean.opBoolean","COPY",EDGE,{"derivedFrom":makeQuery(id+"F3.opExtrude","SWEPT_EDGE",EDGE,{"disambiguationData":[OSD([sQuery(id+"F2.wireOp",EDGE,"E21.0.9.0"),sQuery(id+"F2.wireOp",EDGE,"E21.0.9.3")])]})});
            var Q68;
            Q68=makeQuery(id+"F3.boolean.opBoolean","COPY",EDGE,{"derivedFrom":makeQuery(id+"F3.opExtrude","SWEPT_EDGE",EDGE,{"disambiguationData":[OSD([sQuery(id+"F2.wireOp",EDGE,"E21.0.8.0"),sQuery(id+"F2.wireOp",EDGE,"E21.0.8.3")])]})});
            var Q69;
            Q69=makeQuery(id+"F3.boolean.opBoolean","COPY",EDGE,{"derivedFrom":makeQuery(id+"F3.opExtrude","SWEPT_EDGE",EDGE,{"disambiguationData":[OSD([sQuery(id+"F2.wireOp",EDGE,"E21.0.7.0"),sQuery(id+"F2.wireOp",EDGE,"E21.0.7.3")])]})});
            var Q70;
            Q70=makeQuery(id+"F3.boolean.opBoolean","COPY",EDGE,{"derivedFrom":makeQuery(id+"F3.opExtrude","SWEPT_EDGE",EDGE,{"disambiguationData":[OSD([sQuery(id+"F2.wireOp",EDGE,"E21.0.6.0"),sQuery(id+"F2.wireOp",EDGE,"E21.0.6.3")])]})});
            var Q71;
            Q71=makeQuery(id+"F3.boolean.opBoolean","COPY",EDGE,{"derivedFrom":makeQuery(id+"F3.opExtrude","SWEPT_EDGE",EDGE,{"disambiguationData":[OSD([sQuery(id+"F2.wireOp",EDGE,"E21.0.5.0"),sQuery(id+"F2.wireOp",EDGE,"E21.0.5.3")])]})});
            var Q72;
            Q72=makeQuery(id+"F3.boolean.opBoolean","COPY",EDGE,{"derivedFrom":makeQuery(id+"F3.opExtrude","SWEPT_EDGE",EDGE,{"disambiguationData":[OSD([sQuery(id+"F2.wireOp",EDGE,"E21.0.4.0"),sQuery(id+"F2.wireOp",EDGE,"E21.0.4.3")])]})});
            var Q73;
            Q73=makeQuery(id+"F3.boolean.opBoolean","COPY",EDGE,{"derivedFrom":makeQuery(id+"F3.opExtrude","SWEPT_EDGE",EDGE,{"disambiguationData":[OSD([sQuery(id+"F2.wireOp",EDGE,"E21.0.3.0"),sQuery(id+"F2.wireOp",EDGE,"E21.0.3.3")])]})});
            var Q74;
            Q74=makeQuery(id+"F3.boolean.opBoolean","COPY",EDGE,{"derivedFrom":makeQuery(id+"F3.opExtrude","SWEPT_EDGE",EDGE,{"disambiguationData":[OSD([sQuery(id+"F2.wireOp",EDGE,"E21.0.2.0"),sQuery(id+"F2.wireOp",EDGE,"E21.0.2.3")])]})});
            var Q75;
            Q75=makeQuery(id+"F3.boolean.opBoolean","COPY",EDGE,{"derivedFrom":makeQuery(id+"F3.opExtrude","SWEPT_EDGE",EDGE,{"disambiguationData":[OSD([sQuery(id+"F2.wireOp",EDGE,"E21.0.1.0"),sQuery(id+"F2.wireOp",EDGE,"E21.0.1.3")])]})});
            fillet(context, id + "F4", {"entities" : qUnion([Q0, Q1, Q2, Q3, Q4, Q5, Q6, Q7, Q8, Q9, Q10, Q11, Q12, Q13, Q14, Q15, Q16, Q17, Q18, Q19, Q20, Q21, Q22, Q23, Q24, Q25, Q26, Q27, Q28, Q29, Q30, Q31, Q32, Q33, Q34, Q35, Q36, Q37, Q38, Q39, Q40, Q41, Q42, Q43, Q44, Q45, Q46, Q47, Q48, Q49, Q50, Q51, Q52, Q53, Q54, Q55, Q56, Q57, Q58, Q59, Q60, Q61, Q62, Q63, Q64, Q65, Q66, Q67, Q68, Q69, Q70, Q71, Q72, Q73, Q74, Q75]), "radius" : 6.35 * mm, "tangentPropagation" : true, "allowEdgeOverflow" : false});
        }
        {
            var Q0;
            Q0=makeQuery(id+"F1.opExtrude","SWEPT_FACE",FACE,{"disambiguationData":[OSD([sQuery(id+"F0.wireOp",EDGE,"E14")])]});
            var sketch = newSketch(context, id + "F5", { "sketchPlane" : qUnion([Q0])});
            skPoint(sketch, "E22", {"position": v(-53.98, 1485.9) * mm});
            skPoint(sketch, "E22.positionSnap0", {"position": v(-53.98, 1524) * mm});
            skPoint(sketch, "E23.0.1.0", {"position": v(-53.98, 1257.3) * mm});
            skPoint(sketch, "E23.0.2.0", {"position": v(-53.98, 1028.7) * mm});
            skPoint(sketch, "E23.0.3.0", {"position": v(-53.98, 800.1) * mm});
            skPoint(sketch, "E23.0.4.0", {"position": v(-53.98, 571.5) * mm});
            skPoint(sketch, "E23.0.5.0", {"position": v(-53.98, 342.9) * mm});
            skPoint(sketch, "E23.0.6.0", {"position": v(-53.98, 114.3) * mm});
            skPoint(sketch, "E23.0.7.0", {"position": v(-53.98, -114.3) * mm});
            skPoint(sketch, "E23.0.8.0", {"position": v(-53.98, -342.9) * mm});
            skPoint(sketch, "E23.0.9.0", {"position": v(-53.98, -571.5) * mm});
            skPoint(sketch, "E23.0.10.0", {"position": v(-53.98, -800.1) * mm});
            skPoint(sketch, "E23.0.11.0", {"position": v(-53.98, -1028.7) * mm});
            skPoint(sketch, "E23.0.12.0", {"position": v(-53.98, -1257.3) * mm});
            skPoint(sketch, "E23.0.13.0", {"position": v(-53.98, -1485.9) * mm});
            skLineSegment(sketch, "E23.direction1", {"start": v(-53.98, 1485.9) * mm, "end": v(-28.58, 1485.9) * mm, "construction": true});
            skLineSegment(sketch, "E23.direction2", {"start": v(-53.98, 1485.9) * mm, "end": v(-53.98, 1257.3) * mm, "construction": true});
            skLineSegment(sketch, "E24.MirrorCS", {"start": v(53.98, 1485.9) * mm, "end": v(28.58, 1485.9) * mm, "construction": true});
            skPoint(sketch, "E25.MirrorP", {"position": v(53.98, 800.1) * mm});
            skPoint(sketch, "E26.MirrorP", {"position": v(53.98, 1028.7) * mm});
            skPoint(sketch, "E27.MirrorP", {"position": v(53.98, 1257.3) * mm});
            skPoint(sketch, "E28.MirrorP", {"position": v(53.98, 1485.9) * mm});
            skLineSegment(sketch, "E29.MirrorCS", {"start": v(53.98, 1485.9) * mm, "end": v(53.98, 1257.3) * mm, "construction": true});
            skPoint(sketch, "E30.MirrorP", {"position": v(53.98, 114.3) * mm});
            skPoint(sketch, "E31.MirrorP", {"position": v(53.98, 342.9) * mm});
            skPoint(sketch, "E32.MirrorP", {"position": v(53.98, 571.5) * mm});
            skPoint(sketch, "E33.MirrorP", {"position": v(53.98, -114.3) * mm});
            skPoint(sketch, "E34.MirrorP", {"position": v(53.98, -342.9) * mm});
            skPoint(sketch, "E35.MirrorP", {"position": v(53.98, -1257.3) * mm});
            skPoint(sketch, "E36.MirrorP", {"position": v(53.98, -1028.7) * mm});
            skPoint(sketch, "E37.MirrorP", {"position": v(53.98, -800.1) * mm});
            skPoint(sketch, "E38.MirrorP", {"position": v(53.98, -571.5) * mm});
            skPoint(sketch, "E39.MirrorP", {"position": v(53.98, -1485.9) * mm});
            skSolve(sketch);
        }
        {
            var Q0;
            Q0=sQuery(id+"F5.wireOp",VERTEX,"E23.0.1.0");
            var Q1;
            Q1=sQuery(id+"F5.wireOp",VERTEX,"E22");
            var Q2;
            Q2=sQuery(id+"F5.wireOp",VERTEX,"E25.MirrorP");
            var Q3;
            Q3=sQuery(id+"F5.wireOp",VERTEX,"E23.0.3.0");
            var Q4;
            Q4=sQuery(id+"F5.wireOp",VERTEX,"E23.0.2.0");
            var Q5;
            Q5=sQuery(id+"F5.wireOp",VERTEX,"E32.MirrorP");
            var Q6;
            Q6=sQuery(id+"F5.wireOp",VERTEX,"E23.0.4.0");
            var Q7;
            Q7=sQuery(id+"F5.wireOp",VERTEX,"E31.MirrorP");
            var Q8;
            Q8=sQuery(id+"F5.wireOp",VERTEX,"E30.MirrorP");
            var Q9;
            Q9=sQuery(id+"F5.wireOp",VERTEX,"E23.0.5.0");
            var Q10;
            Q10=sQuery(id+"F5.wireOp",VERTEX,"E23.0.6.0");
            var Q11;
            Q11=sQuery(id+"F5.wireOp",VERTEX,"E26.MirrorP");
            var Q12;
            Q12=sQuery(id+"F5.wireOp",VERTEX,"E28.MirrorP");
            var Q13;
            Q13=sQuery(id+"F5.wireOp",VERTEX,"E27.MirrorP");
            var Q14;
            Q14=sQuery(id+"F5.wireOp",VERTEX,"E23.0.8.0");
            var Q15;
            Q15=sQuery(id+"F5.wireOp",VERTEX,"E36.MirrorP");
            var Q16;
            Q16=sQuery(id+"F5.wireOp",VERTEX,"E23.0.9.0");
            var Q17;
            Q17=sQuery(id+"F5.wireOp",VERTEX,"E39.MirrorP");
            var Q18;
            Q18=sQuery(id+"F5.wireOp",VERTEX,"E37.MirrorP");
            var Q19;
            Q19=sQuery(id+"F5.wireOp",VERTEX,"E23.0.10.0");
            var Q20;
            Q20=sQuery(id+"F5.wireOp",VERTEX,"E38.MirrorP");
            var Q21;
            Q21=sQuery(id+"F5.wireOp",VERTEX,"E23.0.12.0");
            var Q22;
            Q22=sQuery(id+"F5.wireOp",VERTEX,"E23.0.11.0");
            var Q23;
            Q23=sQuery(id+"F5.wireOp",VERTEX,"E33.MirrorP");
            var Q24;
            Q24=sQuery(id+"F5.wireOp",VERTEX,"E35.MirrorP");
            var Q25;
            Q25=sQuery(id+"F5.wireOp",VERTEX,"E23.0.7.0");
            var Q26;
            Q26=sQuery(id+"F5.wireOp",VERTEX,"E23.0.13.0");
            var Q27;
            Q27=sQuery(id+"F5.wireOp",VERTEX,"E34.MirrorP");
            var Q28;
            Q28=makeQuery(id+"F1.opExtrude","SWEPT_BODY",BODY,{"disambiguationData":[OSD([sQuery(id+"F0.wireOp",EDGE,"E0"),sQuery(id+"F0.wireOp",EDGE,"E1"),sQuery(id+"F0.wireOp",EDGE,"E2"),sQuery(id+"F0.wireOp",EDGE,"E3"),sQuery(id+"F0.wireOp",EDGE,"E4"),sQuery(id+"F0.wireOp",EDGE,"E5"),sQuery(id+"F0.wireOp",EDGE,"E6"),sQuery(id+"F0.wireOp",EDGE,"E7.MirrorCS"),sQuery(id+"F0.wireOp",EDGE,"E8.MirrorCS"),sQuery(id+"F0.wireOp",EDGE,"E9.MirrorCS"),sQuery(id+"F0.wireOp",EDGE,"E10.MirrorCS"),sQuery(id+"F0.wireOp",EDGE,"E11.MirrorCS"),sQuery(id+"F0.wireOp",EDGE,"E12.MirrorCS"),sQuery(id+"F0.wireOp",EDGE,"E13"),sQuery(id+"F0.wireOp",EDGE,"E14"),sQuery(id+"F0.wireOp",EDGE,"E16.MirrorCS"),sQuery(id+"F0.wireOp",EDGE,"E17.MirrorCS")])]});
            hole(context, id + "F6", {"style" : HoleStyle.SIMPLE, "endStyle" : HoleEndStyle.THROUGH, "standardTappedOrClearance" : lookupTablePath({ "standard" : "ANSI", "engagement" : "75%", "pitch" : "24 tpi", "size" : "#10", "type" : "Tapped" }), "standardBlindInLast" : lookupTablePath({ "standard" : "ANSI", "engagement" : "75%", "pitch" : "24 tpi", "size" : "#10", "type" : "Tapped" }), "holeDiameter" : 3.8 * mm, "majorDiameter" : 4.83 * mm, "showTappedDepth" : true, "tappedDepth" : 16.5 * mm, "tapClearance" : 3, "startFromSketch" : true, "locations" : qUnion([Q0, Q1, Q2, Q3, Q4, Q5, Q6, Q7, Q8, Q9, Q10, Q11, Q12, Q13, Q14, Q15, Q16, Q17, Q18, Q19, Q20, Q21, Q22, Q23, Q24, Q25, Q26, Q27]), "scope" : qUnion([Q28])});
        }
        {
            var Q0;
            Q0=makeQuery(id+"F1.opExtrude","SWEPT_FACE",FACE,{"disambiguationData":[OSD([sQuery(id+"F0.wireOp",EDGE,"E9.MirrorCS")])]});
            var sketch = newSketch(context, id + "F7", { "sketchPlane" : qUnion([Q0])});
            skPoint(sketch, "E40", {"position": v(65.05, -1485.9) * mm});
            skPoint(sketch, "E40.positionSnap0", {"position": v(65.05, -1524) * mm});
            skPoint(sketch, "E41.0.1.0", {"position": v(65.05, -1257.3) * mm});
            skPoint(sketch, "E41.0.2.0", {"position": v(65.05, -1028.7) * mm});
            skPoint(sketch, "E41.0.3.0", {"position": v(65.05, -800.1) * mm});
            skPoint(sketch, "E41.0.4.0", {"position": v(65.05, -571.5) * mm});
            skPoint(sketch, "E41.0.5.0", {"position": v(65.05, -342.9) * mm});
            skPoint(sketch, "E41.0.6.0", {"position": v(65.05, -114.3) * mm});
            skPoint(sketch, "E41.0.7.0", {"position": v(65.05, 114.3) * mm});
            skPoint(sketch, "E41.0.8.0", {"position": v(65.05, 342.9) * mm});
            skPoint(sketch, "E41.0.9.0", {"position": v(65.05, 571.5) * mm});
            skPoint(sketch, "E41.0.10.0", {"position": v(65.05, 800.1) * mm});
            skPoint(sketch, "E41.0.11.0", {"position": v(65.05, 1028.7) * mm});
            skPoint(sketch, "E41.0.12.0", {"position": v(65.05, 1257.3) * mm});
            skPoint(sketch, "E41.0.13.0", {"position": v(65.05, 1485.9) * mm});
            skLineSegment(sketch, "E41.direction1", {"start": v(65.05, -1485.9) * mm, "end": v(90.45, -1485.9) * mm, "construction": true});
            skLineSegment(sketch, "E41.direction2", {"start": v(65.05, -1485.9) * mm, "end": v(65.05, -1257.3) * mm, "construction": true});
            skSolve(sketch);
        }
        {
            var Q0;
            Q0=makeQuery(id+"F1.opExtrude","SWEPT_FACE",FACE,{"disambiguationData":[OSD([sQuery(id+"F0.wireOp",EDGE,"E3")])]});
            var sketch = newSketch(context, id + "F8", { "sketchPlane" : qUnion([Q0])});
            skPoint(sketch, "E42", {"position": v(-65.05, -1485.9) * mm});
            skPoint(sketch, "E42.positionSnap0", {"position": v(-65.05, -1524) * mm});
            skPoint(sketch, "E43.0.1.0", {"position": v(-65.05, -1257.3) * mm});
            skPoint(sketch, "E43.0.2.0", {"position": v(-65.05, -1028.7) * mm});
            skPoint(sketch, "E43.0.3.0", {"position": v(-65.05, -800.1) * mm});
            skPoint(sketch, "E43.0.4.0", {"position": v(-65.05, -571.5) * mm});
            skPoint(sketch, "E43.0.5.0", {"position": v(-65.05, -342.9) * mm});
            skPoint(sketch, "E43.0.6.0", {"position": v(-65.05, -114.3) * mm});
            skPoint(sketch, "E43.0.7.0", {"position": v(-65.05, 114.3) * mm});
            skPoint(sketch, "E43.0.8.0", {"position": v(-65.05, 342.9) * mm});
            skPoint(sketch, "E43.0.9.0", {"position": v(-65.05, 571.5) * mm});
            skPoint(sketch, "E43.0.10.0", {"position": v(-65.05, 800.1) * mm});
            skPoint(sketch, "E43.0.11.0", {"position": v(-65.05, 1028.7) * mm});
            skPoint(sketch, "E43.0.12.0", {"position": v(-65.05, 1257.3) * mm});
            skPoint(sketch, "E43.0.13.0", {"position": v(-65.05, 1485.9) * mm});
            skLineSegment(sketch, "E43.direction1", {"start": v(-65.05, -1485.9) * mm, "end": v(-39.65, -1485.9) * mm, "construction": true});
            skLineSegment(sketch, "E43.direction2", {"start": v(-65.05, -1485.9) * mm, "end": v(-65.05, -1257.3) * mm, "construction": true});
            skSolve(sketch);
        }
        {
            var Q0;
            Q0=sQuery(id+"F7.wireOp",VERTEX,"E41.0.11.0");
            var Q1;
            Q1=sQuery(id+"F7.wireOp",VERTEX,"E41.0.12.0");
            var Q2;
            Q2=sQuery(id+"F7.wireOp",VERTEX,"E41.0.13.0");
            var Q3;
            Q3=sQuery(id+"F7.wireOp",VERTEX,"E41.0.10.0");
            var Q4;
            Q4=sQuery(id+"F7.wireOp",VERTEX,"E41.0.6.0");
            var Q5;
            Q5=sQuery(id+"F7.wireOp",VERTEX,"E41.0.7.0");
            var Q6;
            Q6=sQuery(id+"F7.wireOp",VERTEX,"E41.0.9.0");
            var Q7;
            Q7=sQuery(id+"F7.wireOp",VERTEX,"E41.0.8.0");
            var Q8;
            Q8=sQuery(id+"F7.wireOp",VERTEX,"E41.direction1.end");
            var Q9;
            Q9=sQuery(id+"F7.wireOp",VERTEX,"E41.0.1.0");
            var Q10;
            Q10=sQuery(id+"F7.wireOp",VERTEX,"E41.0.3.0");
            var Q11;
            Q11=sQuery(id+"F7.wireOp",VERTEX,"E41.direction1.start");
            var Q12;
            Q12=sQuery(id+"F7.wireOp",VERTEX,"E41.0.2.0");
            var Q13;
            Q13=sQuery(id+"F7.wireOp",VERTEX,"E41.0.5.0");
            var Q14;
            Q14=sQuery(id+"F7.wireOp",VERTEX,"E41.0.4.0");
            var Q15;
            Q15=sQuery(id+"F8.wireOp",VERTEX,"E42");
            var Q16;
            Q16=sQuery(id+"F8.wireOp",VERTEX,"E43.0.1.0");
            var Q17;
            Q17=sQuery(id+"F8.wireOp",VERTEX,"E43.0.12.0");
            var Q18;
            Q18=sQuery(id+"F8.wireOp",VERTEX,"E43.0.13.0");
            var Q19;
            Q19=sQuery(id+"F8.wireOp",VERTEX,"E43.0.8.0");
            var Q20;
            Q20=sQuery(id+"F8.wireOp",VERTEX,"E43.0.9.0");
            var Q21;
            Q21=sQuery(id+"F8.wireOp",VERTEX,"E43.0.10.0");
            var Q22;
            Q22=sQuery(id+"F8.wireOp",VERTEX,"E43.0.7.0");
            var Q23;
            Q23=sQuery(id+"F8.wireOp",VERTEX,"E43.0.11.0");
            var Q24;
            Q24=sQuery(id+"F8.wireOp",VERTEX,"E43.0.4.0");
            var Q25;
            Q25=sQuery(id+"F8.wireOp",VERTEX,"E43.0.5.0");
            var Q26;
            Q26=sQuery(id+"F8.wireOp",VERTEX,"E43.0.2.0");
            var Q27;
            Q27=sQuery(id+"F8.wireOp",VERTEX,"E43.0.3.0");
            var Q28;
            Q28=sQuery(id+"F8.wireOp",VERTEX,"E43.0.6.0");
            var Q29;
            Q29=makeQuery(id+"F1.opExtrude","SWEPT_BODY",BODY,{"disambiguationData":[OSD([sQuery(id+"F0.wireOp",EDGE,"E0"),sQuery(id+"F0.wireOp",EDGE,"E1"),sQuery(id+"F0.wireOp",EDGE,"E2"),sQuery(id+"F0.wireOp",EDGE,"E3"),sQuery(id+"F0.wireOp",EDGE,"E4"),sQuery(id+"F0.wireOp",EDGE,"E5"),sQuery(id+"F0.wireOp",EDGE,"E6"),sQuery(id+"F0.wireOp",EDGE,"E7.MirrorCS"),sQuery(id+"F0.wireOp",EDGE,"E8.MirrorCS"),sQuery(id+"F0.wireOp",EDGE,"E9.MirrorCS"),sQuery(id+"F0.wireOp",EDGE,"E10.MirrorCS"),sQuery(id+"F0.wireOp",EDGE,"E11.MirrorCS"),sQuery(id+"F0.wireOp",EDGE,"E12.MirrorCS"),sQuery(id+"F0.wireOp",EDGE,"E13"),sQuery(id+"F0.wireOp",EDGE,"E14"),sQuery(id+"F0.wireOp",EDGE,"E16.MirrorCS"),sQuery(id+"F0.wireOp",EDGE,"E17.MirrorCS")])]});
            hole(context, id + "F9", {"style" : HoleStyle.C_SINK, "endStyle" : HoleEndStyle.THROUGH, "standardTappedOrClearance" : lookupTablePath({ "standard" : "ANSI", "fit" : "Normal (ASME)", "size" : "1/4", "type" : "Clearance" }), "standardBlindInLast" : lookupTablePath({ "fit" : "Free", "standard" : "ANSI", "size" : "1/4", "type" : "Clearance" }), "holeDiameter" : 6.76 * mm, "cSinkDiameter" : 13.5 * mm, "cSinkAngle" : 82 * degree, "majorDiameter" : 6.35 * mm, "tappedDepth" : 16.5 * mm, "tapClearance" : 3, "startFromSketch" : true, "locations" : qUnion([Q0, Q1, Q2, Q3, Q4, Q5, Q6, Q7, Q8, Q9, Q10, Q11, Q12, Q13, Q14, Q15, Q16, Q17, Q18, Q19, Q20, Q21, Q22, Q23, Q24, Q25, Q26, Q27, Q28]), "scope" : qUnion([Q29])});
        }
    });
